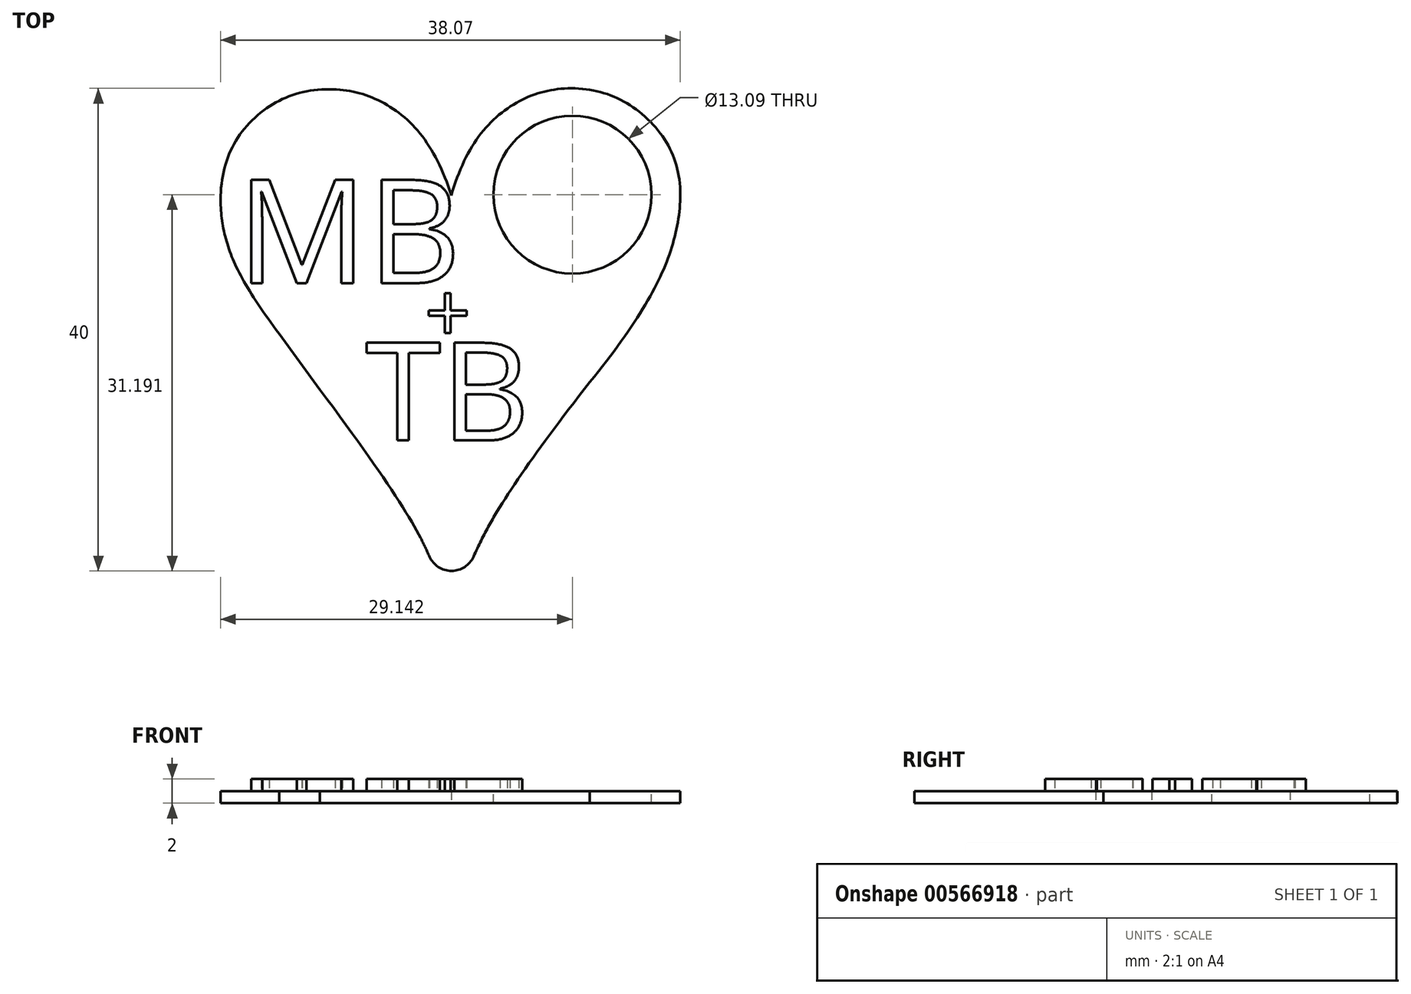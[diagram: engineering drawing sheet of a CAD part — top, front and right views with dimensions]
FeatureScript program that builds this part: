
annotation { "Feature Type Name" : "Feature", "Feature Type Description" : "" }
export const myFeature = defineFeature(function(context is Context, id is Id, definition is map)
    precondition{}
    {
        {
            var Q0;
            Q0=qCreatedBy(makeId("Top.planeOp"),FACE);
            var sketch = newSketch(context, id + "F0", { "sketchPlane" : qUnion([Q0])});
            skText(sketch, "E0", { "text": "♥", "fontName": "Tinos-Bold.ttf"});
            const initialGuessF0  = {"E0": [-0.04672, 0, 1, 0, 0.05548]};
            skSetInitialGuess(sketch, initialGuessF0);
            skSolve(sketch);
        }
        {
            var Q0;
            Q0 = qSketchRegion(id + "F0", true);
            var Q1;
            Q1 = qConstructionFilter(qBodyType(qCreatedBy(id + "F0" ,EDGE), BodyType.WIRE), ConstructionObject.NO);
            extrude(context, id + "F1", {"entities" : qUnion([Q0]), "surfaceEntities" : qUnion([Q1]), "depth" : 1 * mm, "offsetDistance" : 25 * mm});
        }
        {
            var Q0;
            Q0=makeQuery(id+"F1.opExtrude","CAP_FACE",FACE,{"disambiguationData":[OSD([sQuery(id+"F0.wireOp",EDGE,"E0.sketch_text.stroke-0"),sQuery(id+"F0.wireOp",EDGE,"E0.sketch_text.stroke-1"),sQuery(id+"F0.wireOp",EDGE,"E0.sketch_text.stroke-2"),sQuery(id+"F0.wireOp",EDGE,"E0.sketch_text.stroke-3"),sQuery(id+"F0.wireOp",EDGE,"E0.sketch_text.stroke-4"),sQuery(id+"F0.wireOp",EDGE,"E0.sketch_text.stroke-5"),sQuery(id+"F0.wireOp",EDGE,"E0.sketch_text.stroke-6"),sQuery(id+"F0.wireOp",EDGE,"E0.sketch_text.stroke-7"),sQuery(id+"F0.wireOp",EDGE,"E0.sketch_text.stroke-8"),sQuery(id+"F0.wireOp",EDGE,"E0.sketch_text.stroke-9"),sQuery(id+"F0.wireOp",EDGE,"E0.sketch_text.stroke-10"),sQuery(id+"F0.wireOp",EDGE,"E0.sketch_text.stroke-11"),sQuery(id+"F0.wireOp",EDGE,"E0.sketch_text.stroke-12"),sQuery(id+"F0.wireOp",EDGE,"E0.sketch_text.stroke-13"),sQuery(id+"F0.wireOp",EDGE,"E0.sketch_text.stroke-14"),sQuery(id+"F0.wireOp",EDGE,"E0.sketch_text.stroke-15"),sQuery(id+"F0.wireOp",EDGE,"E0.sketch_text.stroke-16")])],"isStart":false});
            var sketch = newSketch(context, id + "F2", { "sketchPlane" : qUnion([Q0])});
            skText(sketch, "E1", { "text": "TB", "fontName": "OpenSans-Regular.ttf"});
            skText(sketch, "E2", { "text": "+", "fontName": "OpenSans-Regular.ttf"});
            skText(sketch, "E3", { "text": "MB", "fontName": "OpenSans-Regular.ttf"});
            const initialGuessF2  = {"E1": [-0.03089, 0.0139, 1, 0, 0.00816], "E2": [-0.026, 0.02206, 1, 0, 0.00487], "E3": [-0.04153, 0.02694, 1, 0, 0.00862]};
            skSetInitialGuess(sketch, initialGuessF2);
            skSolve(sketch);
        }
        {
            var Q0;
            Q0 = qSketchRegion(id + "F2", true);
            extrude(context, id + "F3", {"entities" : qUnion([Q0]), "operationType" : NewBodyOperationType.ADD, "depth" : 1 * mm, "offsetDistance" : 25 * mm});
        }
        {
            var Q0;
            {var subQ0=sQuery(id+"F0.wireOp",EDGE,"E0.sketch_text.stroke-8");var subQ1=sQuery(id+"F0.wireOp",EDGE,"E0.sketch_text.stroke-7");var subQ2=sQuery(id+"F0.wireOp",EDGE,"E0.sketch_text.stroke-6");var subQ3=sQuery(id+"F0.wireOp",EDGE,"E0.sketch_text.stroke-5");var subQ4=sQuery(id+"F0.wireOp",EDGE,"E0.sketch_text.stroke-4");var subQ5=sQuery(id+"F0.wireOp",EDGE,"E0.sketch_text.stroke-9");var subQ6=sQuery(id+"F0.wireOp",EDGE,"E0.sketch_text.stroke-0");var subQ7=sQuery(id+"F0.wireOp",EDGE,"E0.sketch_text.stroke-3");var subQ8=sQuery(id+"F0.wireOp",EDGE,"E0.sketch_text.stroke-1");var subQ9=sQuery(id+"F0.wireOp",EDGE,"E0.sketch_text.stroke-2");var subQ10=sQuery(id+"F0.wireOp",EDGE,"E0.sketch_text.stroke-16");var subQ11=sQuery(id+"F0.wireOp",EDGE,"E0.sketch_text.stroke-10");var subQ12=sQuery(id+"F0.wireOp",EDGE,"E0.sketch_text.stroke-11");var subQ13=sQuery(id+"F0.wireOp",EDGE,"E0.sketch_text.stroke-12");var subQ14=sQuery(id+"F0.wireOp",EDGE,"E0.sketch_text.stroke-13");var subQ15=sQuery(id+"F0.wireOp",EDGE,"E0.sketch_text.stroke-14");var subQ16=sQuery(id+"F0.wireOp",EDGE,"E0.sketch_text.stroke-15");Q0=makeQuery(id+"F3.boolean.opBoolean","SPLIT",FACE,{"disambiguationData":[TD([makeQuery(id+"F1.opExtrude","SWEPT_FACE",FACE,{"disambiguationData":[OSD([subQ6])]})])],"derivedFrom":makeQuery(id+"F1.opExtrude","CAP_FACE",FACE,{"disambiguationData":[OSD([subQ6,subQ8,subQ9,subQ7,subQ4,subQ3,subQ2,subQ1,subQ0,subQ5,subQ11,subQ12,subQ13,subQ14,subQ15,subQ16,subQ10])],"isStart":false})});}
            var sketch = newSketch(context, id + "F4", { "sketchPlane" : qUnion([Q0])});
            skCircle(sketch, "E4", {"center": v(-13.74, 34.27) * mm, "radius": 6.54 * mm});
            skSolve(sketch);
        }
        {
            var Q0;
            Q0=makeQuery(id+"F4.imprint","IMPRINT",FACE,{"disambiguationData":[TD([[makeQuery(id+"F4.imprint","IMPRINT",EDGE,{"derivedFrom":sQuery(id+"F4.wireOp",EDGE,"E4")}),1.0]])]});
            extrude(context, id + "F5", {"entities" : qUnion([Q0]), "operationType" : NewBodyOperationType.REMOVE, "oppositeDirection" : true, "depth" : 25 * mm, "offsetDistance" : 25 * mm});
        }
        {
            var Q0;
            Q0=makeQuery(id+"F1.opExtrude","SWEPT_EDGE",EDGE,{"disambiguationData":[OSD([sQuery(id+"F0.wireOp",EDGE,"E0.sketch_text.stroke-0"),sQuery(id+"F0.wireOp",EDGE,"E0.sketch_text.stroke-16")])]});
            fillet(context, id + "F6", {"entities" : qUnion([Q0]), "radius" : 2 * mm, "tangentPropagation" : true, "allowEdgeOverflow" : false});
        }
    });
